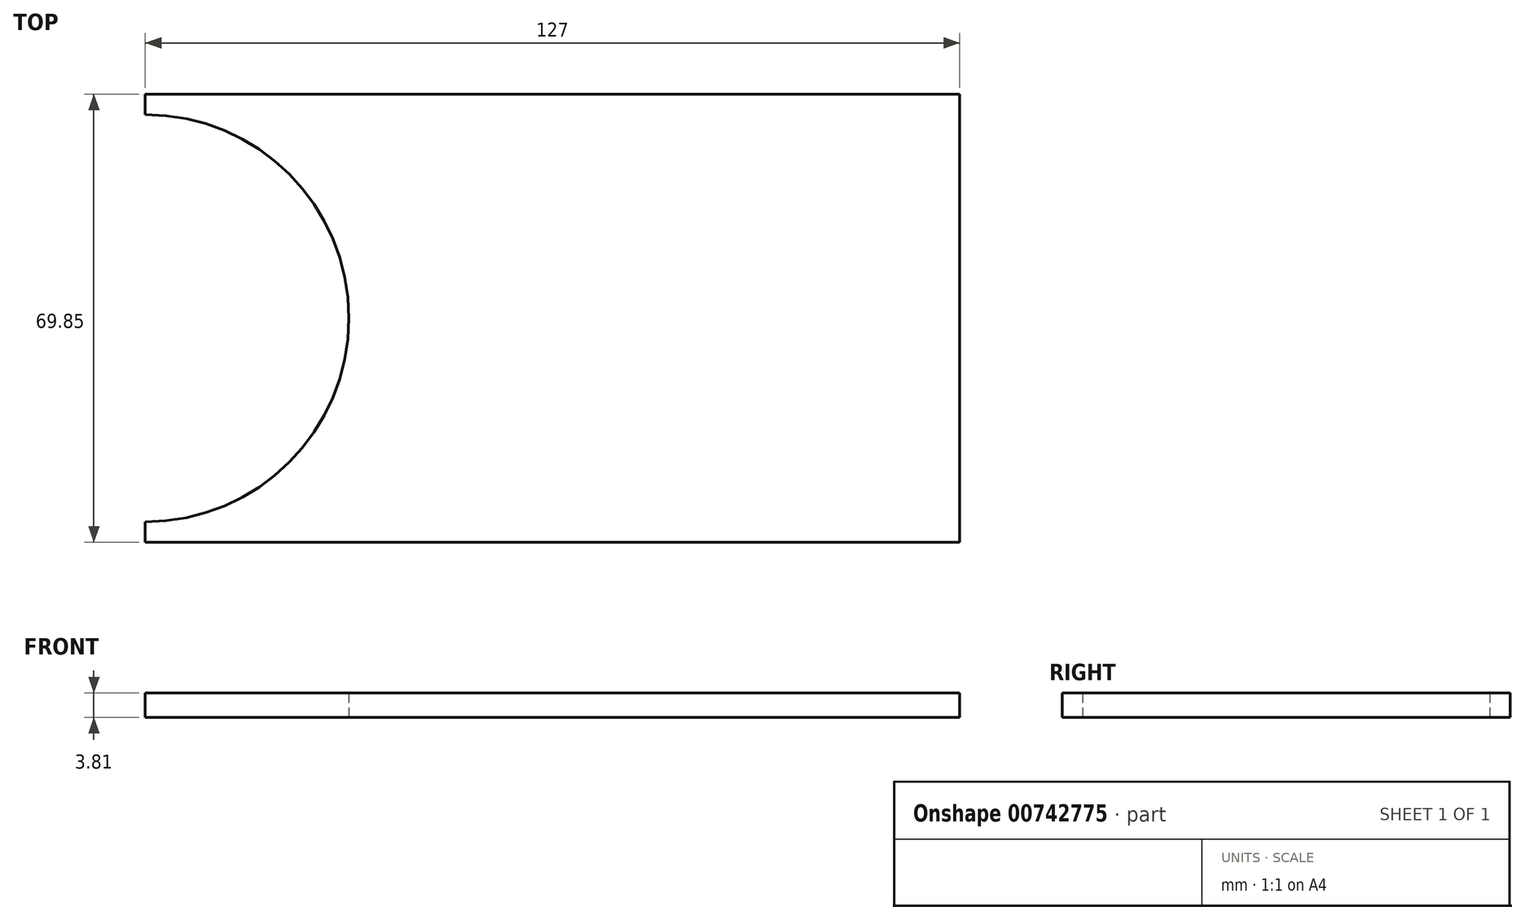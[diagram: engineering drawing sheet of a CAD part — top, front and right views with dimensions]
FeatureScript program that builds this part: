
annotation { "Feature Type Name" : "Feature", "Feature Type Description" : "" }
export const myFeature = defineFeature(function(context is Context, id is Id, definition is map)
    precondition{}
    {
        {
            var Q0;
            Q0=qCreatedBy(makeId("Top.planeOp"),FACE);
            var sketch = newSketch(context, id + "F0", { "sketchPlane" : qUnion([Q0])});
            skLineSegment(sketch, "E0.bottom", {"start": v(-79.32, 43.97) * mm, "end": v(47.68, 43.97) * mm});
            skLineSegment(sketch, "E0.top", {"start": v(-79.32, -25.88) * mm, "end": v(47.68, -25.88) * mm});
            skLineSegment(sketch, "E0.left", {"start": v(-79.32, 43.97) * mm, "end": v(-79.32, 40.8) * mm});
            skLineSegment(sketch, "E0.right", {"start": v(47.68, 43.97) * mm, "end": v(47.68, -25.88) * mm});
            skArc(sketch, "E1", {"start": v(-79.32, -22.7) * mm, "mid": v(-47.57, 9.04) * mm, "end": v(-79.32, 40.8) * mm});
            skLineSegment(sketch, "E2.trimOffspring", {"start": v(-79.32, -22.7) * mm, "end": v(-79.32, -25.88) * mm});
            skSolve(sketch);
        }
        {
            var Q0;
            Q0=makeQuery(id+"F0.imprint","IMPRINT",FACE,{"disambiguationData":[TD([[makeQuery(id+"F0.imprint","IMPRINT",EDGE,{"derivedFrom":sQuery(id+"F0.wireOp",EDGE,"E0.bottom")}),-1.0]])]});
            extrude(context, id + "F1", {"entities" : qUnion([Q0]), "depth" : 3.8 * mm, "offsetDistance" : 25.4 * mm});
        }
    });
